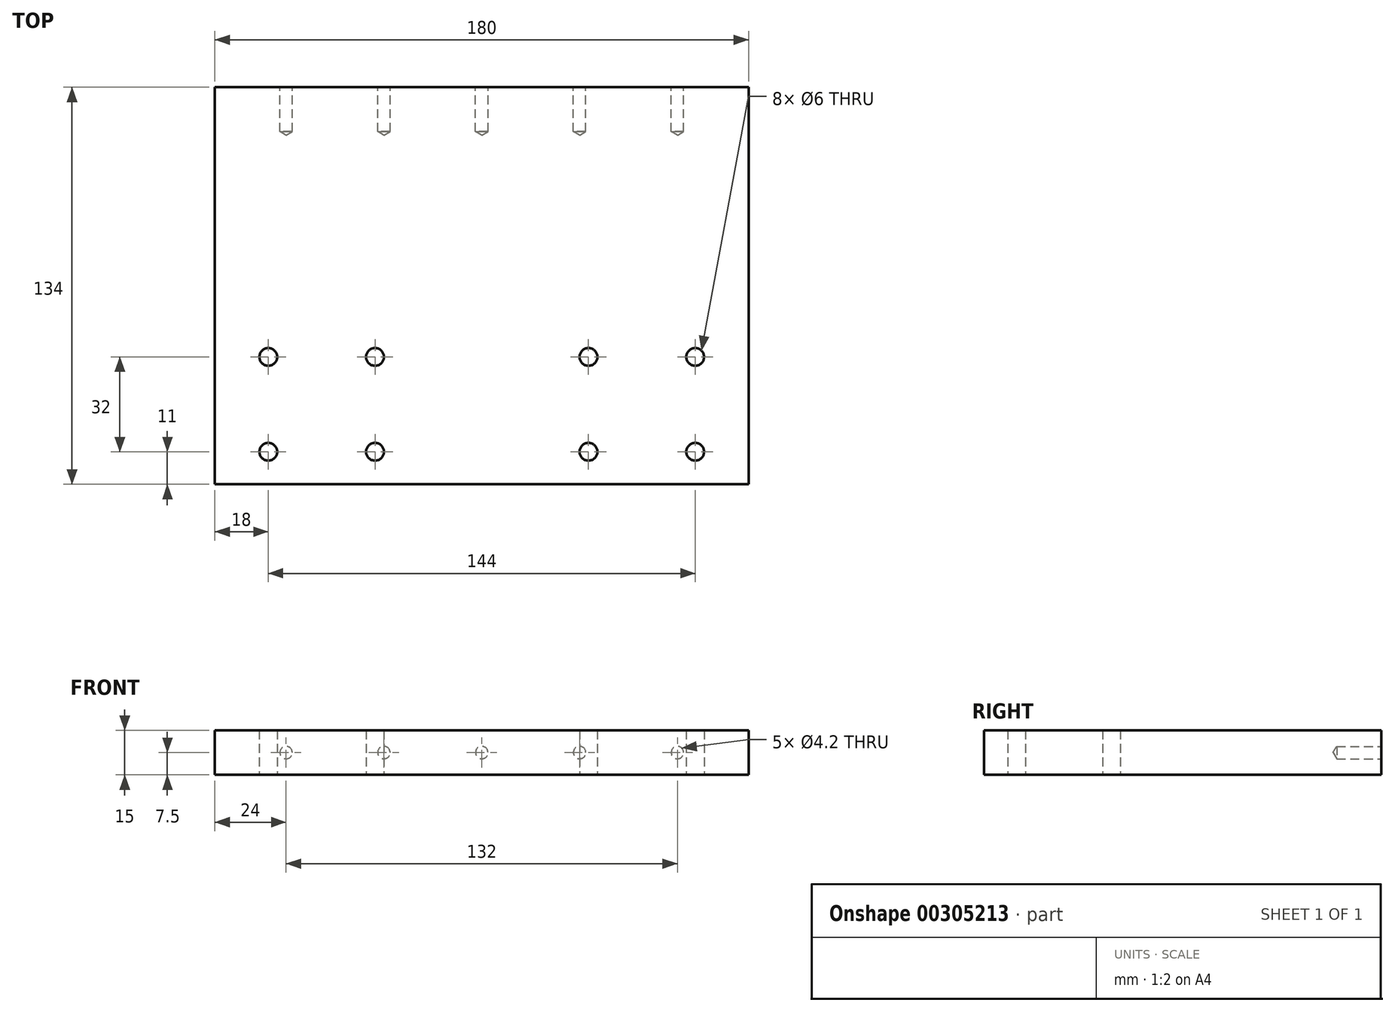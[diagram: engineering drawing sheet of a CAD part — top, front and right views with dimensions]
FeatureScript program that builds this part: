
annotation { "Feature Type Name" : "Feature", "Feature Type Description" : "" }
export const myFeature = defineFeature(function(context is Context, id is Id, definition is map)
    precondition{}
    {
        {
            var Q0;
            Q0=qCreatedBy(makeId("Right.planeOp"),FACE);
            var sketch = newSketch(context, id + "F0", { "sketchPlane" : qUnion([Q0])});
            skLineSegment(sketch, "E0.bottom", {"start": v(0, 0) * mm, "end": v(129, 0) * mm});
            skLineSegment(sketch, "E0.top", {"start": v(0, 15) * mm, "end": v(129, 15) * mm});
            skLineSegment(sketch, "E0.left", {"start": v(0, 0) * mm, "end": v(0, 15) * mm});
            skLineSegment(sketch, "E0.right", {"start": v(129, 0) * mm, "end": v(129, 15) * mm});
            skSolve(sketch);
        }
        {
            var Q0;
            Q0 = qSketchRegion(id + "F0", true);
            var Q1;
            Q1=makeQuery(id+"F0.imprint","IMPRINT",FACE,{"disambiguationData":[TD([[makeQuery(id+"F0.imprint","IMPRINT",EDGE,{"derivedFrom":sQuery(id+"F0.wireOp",EDGE,"E0.bottom")}),1.0]])]});
            extrude(context, id + "F1", {"entities" : qUnion([Q0, Q1]), "depth" : 170 * mm});
        }
        {
            var Q0;
            Q0=makeQuery(id+"F1.opExtrude","SWEPT_FACE",FACE,{"disambiguationData":[OSD([sQuery(id+"F0.wireOp",EDGE,"E0.bottom")])]});
            var sketch = newSketch(context, id + "F2", { "sketchPlane" : qUnion([Q0])});
            skPoint(sketch, "E1", {"position": v(13, -6) * mm});
            skPoint(sketch, "E2", {"position": v(157, -6) * mm});
            skPoint(sketch, "E3", {"position": v(49, -6) * mm});
            skPoint(sketch, "E4", {"position": v(121, -6) * mm});
            skPoint(sketch, "E5", {"position": v(121, -38) * mm});
            skPoint(sketch, "E6", {"position": v(157, -38) * mm});
            skPoint(sketch, "E7", {"position": v(49, -38) * mm});
            skPoint(sketch, "E8", {"position": v(13, -38) * mm});
            skSolve(sketch);
        }
        {
            var Q0;
            Q0=sQuery(id+"F2.wireOp",VERTEX,"E1");
            var Q1;
            Q1=sQuery(id+"F2.wireOp",VERTEX,"E8");
            var Q2;
            Q2=sQuery(id+"F2.wireOp",VERTEX,"E3");
            var Q3;
            Q3=sQuery(id+"F2.wireOp",VERTEX,"E7");
            var Q4;
            Q4=sQuery(id+"F2.wireOp",VERTEX,"E5");
            var Q5;
            Q5=sQuery(id+"F2.wireOp",VERTEX,"E4");
            var Q6;
            Q6=sQuery(id+"F2.wireOp",VERTEX,"E2");
            var Q7;
            Q7=sQuery(id+"F2.wireOp",VERTEX,"E6");
            var Q8;
            Q8=makeQuery(id+"F1.opExtrude","SWEPT_BODY",BODY,{"disambiguationData":[OSD([sQuery(id+"F0.wireOp",EDGE,"E0.bottom"),sQuery(id+"F0.wireOp",EDGE,"E0.top"),sQuery(id+"F0.wireOp",EDGE,"E0.left"),sQuery(id+"F0.wireOp",EDGE,"E0.right")])]});
            hole(context, id + "F3", {"style" : HoleStyle.SIMPLE, "endStyle" : HoleEndStyle.THROUGH, "holeDiameter" : 6 * mm, "tappedDepth" : 12.6 * mm, "tapClearance" : 3, "startFromSketch" : true, "locations" : qUnion([Q0, Q1, Q2, Q3, Q4, Q5, Q6, Q7]), "scope" : qUnion([Q8])});
        }
        {
            var Q0;
            Q0=makeQuery(id+"F1.opExtrude","SWEPT_FACE",FACE,{"disambiguationData":[OSD([sQuery(id+"F0.wireOp",EDGE,"E0.right")])]});
            var sketch = newSketch(context, id + "F4", { "sketchPlane" : qUnion([Q0])});
            skPoint(sketch, "E9", {"position": v(-151, 7.5) * mm});
            skPoint(sketch, "E10", {"position": v(-118, 7.5) * mm});
            skPoint(sketch, "E11", {"position": v(-85, 7.5) * mm});
            skPoint(sketch, "E12", {"position": v(-52, 7.5) * mm});
            skPoint(sketch, "E13", {"position": v(-19, 7.5) * mm});
            skSolve(sketch);
        }
        {
            var Q0;
            Q0=sQuery(id+"F4.wireOp",VERTEX,"E9");
            var Q1;
            Q1=sQuery(id+"F4.wireOp",VERTEX,"E11");
            var Q2;
            Q2=sQuery(id+"F4.wireOp",VERTEX,"E10");
            var Q3;
            Q3=sQuery(id+"F4.wireOp",VERTEX,"E12");
            var Q4;
            Q4=sQuery(id+"F4.wireOp",VERTEX,"E13");
            var Q5;
            Q5=makeQuery(id+"F1.opExtrude","SWEPT_BODY",BODY,{"disambiguationData":[OSD([sQuery(id+"F0.wireOp",EDGE,"E0.bottom"),sQuery(id+"F0.wireOp",EDGE,"E0.top"),sQuery(id+"F0.wireOp",EDGE,"E0.left"),sQuery(id+"F0.wireOp",EDGE,"E0.right")])]});
            hole(context, id + "F5", {"style" : HoleStyle.SIMPLE, "endStyle" : HoleEndStyle.BLIND, "standardTappedOrClearance" : lookupTablePath({ "standard" : "ISO", "engagement" : "75%", "pitch" : "0.8 mm", "size" : "M5", "type" : "Tapped" }), "standardBlindInLast" : lookupTablePath({ "standard" : "ISO", "engagement" : "75%", "pitch" : "0.8 mm", "size" : "M5", "type" : "Tapped" }), "holeDiameter" : 4.2 * mm, "showTappedDepth" : true, "holeDepth" : 15 * mm, "tappedDepth" : 12.6 * mm, "tapClearance" : 3, "startFromSketch" : true, "locations" : qUnion([Q0, Q1, Q2, Q3, Q4]), "scope" : qUnion([Q5]), "majorDiameter" : 5 * mm});
        }
        {
            var Q0;
            Q0=makeQuery(id+"F1.opExtrude","CAP_FACE",FACE,{"disambiguationData":[OSD([sQuery(id+"F0.wireOp",EDGE,"E0.bottom"),sQuery(id+"F0.wireOp",EDGE,"E0.top"),sQuery(id+"F0.wireOp",EDGE,"E0.left"),sQuery(id+"F0.wireOp",EDGE,"E0.right")])],"isStart":false});
            extrude(context, id + "F6", {"entities" : qUnion([Q0]), "operationType" : NewBodyOperationType.ADD, "depth" : 5 * mm});
        }
        {
            var Q0;
            Q0=makeQuery(id+"F1.opExtrude","CAP_FACE",FACE,{"disambiguationData":[OSD([sQuery(id+"F0.wireOp",EDGE,"E0.bottom"),sQuery(id+"F0.wireOp",EDGE,"E0.top"),sQuery(id+"F0.wireOp",EDGE,"E0.left"),sQuery(id+"F0.wireOp",EDGE,"E0.right")])],"isStart":true});
            extrude(context, id + "F7", {"entities" : qUnion([Q0]), "operationType" : NewBodyOperationType.ADD, "depth" : 5 * mm});
        }
        {
            var Q0;
            {var subQ0=sQuery(id+"F0.wireOp",EDGE,"E0.left");Q0=makeQuery(id+"F7.boolean.opBoolean","MERGE",FACE,{"derivedFrom":[makeQuery(id+"F6.boolean.opBoolean","MERGE",FACE,{"derivedFrom":[makeQuery(id+"F1.opExtrude","SWEPT_FACE",FACE,{"disambiguationData":[OSD([subQ0])]}),makeQuery(id+"F6.opExtrude","SWEPT_FACE",FACE,{"disambiguationData":[OSD([subQ0])]})]}),makeQuery(id+"F7.opExtrude","SWEPT_FACE",FACE,{"disambiguationData":[OSD([subQ0])]})]});}
            extrude(context, id + "F8", {"entities" : qUnion([Q0]), "operationType" : NewBodyOperationType.ADD, "depth" : 5 * mm});
        }
    });
